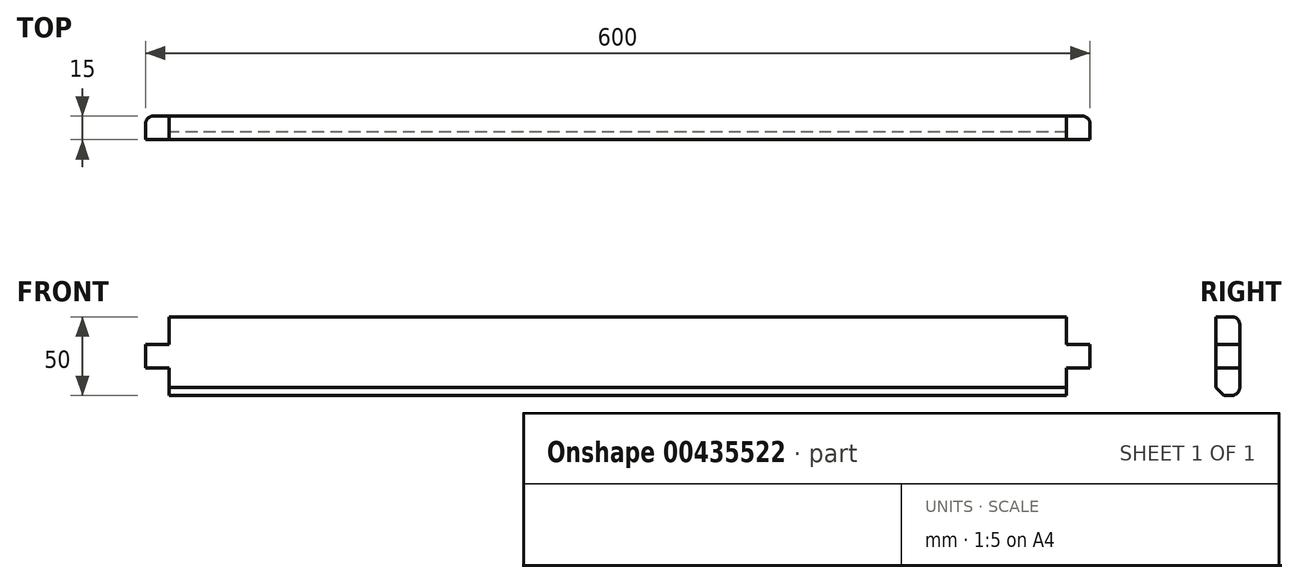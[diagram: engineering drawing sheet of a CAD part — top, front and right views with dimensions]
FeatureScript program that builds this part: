
annotation { "Feature Type Name" : "Feature", "Feature Type Description" : "" }
export const myFeature = defineFeature(function(context is Context, id is Id, definition is map)
    precondition{}
    {
        {
            var Q0;
            Q0=qCreatedBy(makeId("Front.planeOp"),FACE);
            var sketch = newSketch(context, id + "F0", { "sketchPlane" : qUnion([Q0])});
            skLineSegment(sketch, "E0.bottom", {"start": v(0, 0) * mm, "end": v(-285, 0) * mm});
            skLineSegment(sketch, "E0.top", {"start": v(0, -50) * mm, "end": v(-285, -50) * mm});
            skLineSegment(sketch, "E1", {"start": v(-285, -32.5) * mm, "end": v(-300, -32.5) * mm});
            skLineSegment(sketch, "E2", {"start": v(-300, -32.5) * mm, "end": v(-300, -17.5) * mm});
            skLineSegment(sketch, "E3", {"start": v(-300, -17.5) * mm, "end": v(-285, -17.5) * mm});
            skLineSegment(sketch, "E4", {"start": v(-285, 0) * mm, "end": v(-285, -17.5) * mm});
            skLineSegment(sketch, "E5", {"start": v(-285, -32.5) * mm, "end": v(-285, -50) * mm});
            skLineSegment(sketch, "E6.MirrorCS", {"start": v(285, 0) * mm, "end": v(285, -17.5) * mm});
            skLineSegment(sketch, "E7.MirrorCS", {"start": v(300, -32.5) * mm, "end": v(300, -17.5) * mm});
            skLineSegment(sketch, "E8.MirrorCS", {"start": v(285, -32.5) * mm, "end": v(285, -50) * mm});
            skLineSegment(sketch, "E9.MirrorCS", {"start": v(285, -32.5) * mm, "end": v(300, -32.5) * mm});
            skLineSegment(sketch, "E10.MirrorCS", {"start": v(300, -17.5) * mm, "end": v(285, -17.5) * mm});
            skLineSegment(sketch, "E11.MirrorCS", {"start": v(0, 0) * mm, "end": v(285, 0) * mm});
            skLineSegment(sketch, "E12.MirrorCS", {"start": v(0, -50) * mm, "end": v(285, -50) * mm});
            skSolve(sketch);
        }
        {
            var Q0;
            Q0=makeQuery(id+"F0.imprint","IMPRINT",FACE,{"disambiguationData":[TD([[makeQuery(id+"F0.imprint","IMPRINT",EDGE,{"derivedFrom":sQuery(id+"F0.wireOp",EDGE,"E0.bottom")}),1.0]])]});
            extrude(context, id + "F1", {"entities" : qUnion([Q0]), "depth" : 15 * mm});
        }
        {
            var Q0;
            Q0=makeQuery(id+"F1.opExtrude","CAP_EDGE",EDGE,{"disambiguationData":[OSD([sQuery(id+"F0.wireOp",EDGE,"E7.MirrorCS")])],"isStart":true});
            var Q1;
            Q1=makeQuery(id+"F1.opExtrude","CAP_EDGE",EDGE,{"disambiguationData":[OSD([sQuery(id+"F0.wireOp",EDGE,"E2")])],"isStart":true});
            fillet(context, id + "F2", {"entities" : qUnion([Q0, Q1]), "radius" : 5 * mm, "tangentPropagation" : true, "allowEdgeOverflow" : false});
        }
        {
            var Q0;
            Q0=makeQuery(id+"F1.opExtrude","CAP_EDGE",EDGE,{"disambiguationData":[OSD([sQuery(id+"F0.wireOp",EDGE,"E0.bottom"),sQuery(id+"F0.wireOp",EDGE,"E11.MirrorCS")])],"isStart":true});
            var Q1;
            Q1=makeQuery(id+"F1.opExtrude","CAP_EDGE",EDGE,{"disambiguationData":[OSD([sQuery(id+"F0.wireOp",EDGE,"E0.top"),sQuery(id+"F0.wireOp",EDGE,"E12.MirrorCS")])],"isStart":true});
            fillet(context, id + "F3", {"entities" : qUnion([Q0, Q1]), "radius" : 5 * mm, "tangentPropagation" : true, "allowEdgeOverflow" : false});
        }
        {
            var Q0;
            Q0=makeQuery(id+"F1.opExtrude","CAP_EDGE",EDGE,{"disambiguationData":[OSD([sQuery(id+"F0.wireOp",EDGE,"E0.top"),sQuery(id+"F0.wireOp",EDGE,"E12.MirrorCS")])],"isStart":false});
            chamfer(context, id + "F4", {"entities" : qUnion([Q0]), "width" : 5 * mm, "tangentPropagation" : true});
        }
    });
